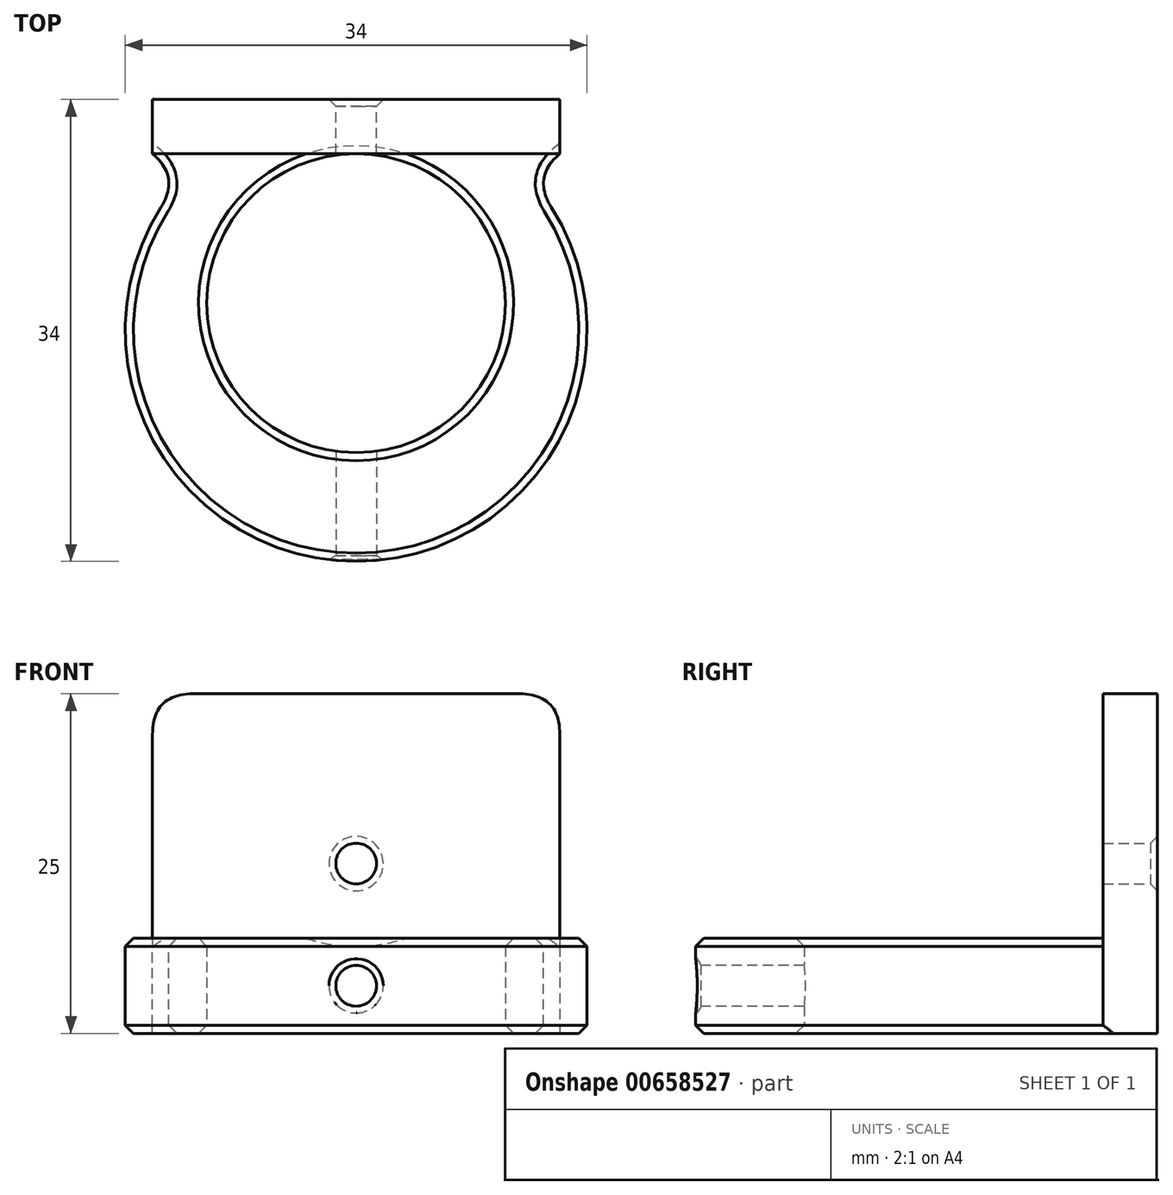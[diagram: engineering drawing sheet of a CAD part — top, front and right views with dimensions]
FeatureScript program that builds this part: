
annotation { "Feature Type Name" : "Feature", "Feature Type Description" : "" }
export const myFeature = defineFeature(function(context is Context, id is Id, definition is map)
    precondition{}
    {
        {
            var Q0;
            Q0=qCreatedBy(makeId("Top.planeOp"),FACE);
            var sketch = newSketch(context, id + "F0", { "sketchPlane" : qUnion([Q0])});
            skCircle(sketch, "E0", {"center": v(0, 0) * mm, "radius": 11 * mm});
            skLineSegment(sketch, "E1.bottom", {"start": v(-15, 15) * mm, "end": v(15, 15) * mm});
            skLineSegment(sketch, "E1.top", {"start": v(-15, 11) * mm, "end": v(15, 11) * mm});
            skLineSegment(sketch, "E1.left", {"start": v(-15, 15) * mm, "end": v(-15, 11) * mm});
            skLineSegment(sketch, "E1.right", {"start": v(15, 15) * mm, "end": v(15, 11) * mm});
            skPoint(sketch, "E2", {"position": v(0, 15) * mm});
            skCircle(sketch, "E3", {"center": v(0, -2) * mm, "radius": 17 * mm});
            skPoint(sketch, "E4", {"position": v(0, -11) * mm});
            skPoint(sketch, "E5", {"position": v(0, -19) * mm});
            skPoint(sketch, "E6", {"position": v(0, 11) * mm});
            skSolve(sketch);
        }
        {
            var Q0;
            {var subQ5=sQuery(id+"F0.wireOp",EDGE,"E1.right");Q0=makeQuery(id+"F0.imprint","IMPRINT",FACE,{"disambiguationData":[TD([[makeQuery(id+"F0.imprint","IMPRINT",EDGE,{"derivedFrom":subQ5}),-1.0]])]});}
            var Q1;
            {var subQ0=sQuery(id+"F0.wireOp",EDGE,"8q8d3DDL-PRP0-A8uf-fQ6a-dR3t6nBeqXp1");var subQ1=makeQuery(id+"F0.imprint","INTERSECT",VERTEX,{"derivedFrom":[subQ0,sQuery(id+"F0.wireOp",EDGE,"E1.bottom")]});Q1=makeQuery(id+"F0.imprint","IMPRINT",FACE,{"disambiguationData":[TD([[makeQuery(id+"F0.imprint","IMPRINT",EDGE,{"disambiguationData":[TD([[subQ1,1.0]])],"derivedFrom":subQ0}),1.0]])]});}
            var Q2;
            {var subQ5=sQuery(id+"F0.wireOp",EDGE,"E1.left");Q2=makeQuery(id+"F0.imprint","IMPRINT",FACE,{"disambiguationData":[TD([[makeQuery(id+"F0.imprint","IMPRINT",EDGE,{"derivedFrom":subQ5}),1.0]])]});}
            var Q3;
            {var subQ0=sQuery(id+"F0.wireOp",EDGE,"E0");Q3=makeQuery(id+"F0.imprint","IMPRINT",FACE,{"disambiguationData":[TD([[makeQuery(id+"F0.imprint","IMPRINT",EDGE,{"derivedFrom":subQ0}),-1.0]])]});}
            var Q4;
            {var subQ0=sQuery(id+"F0.wireOp",EDGE,"E1.top");var subQ1=makeQuery(id+"F0.imprint","INTERSECT",VERTEX,{"derivedFrom":[sQuery(id+"F0.wireOp",EDGE,"E0"),subQ0]});Q4=makeQuery(id+"F0.imprint","IMPRINT",FACE,{"disambiguationData":[TD([[makeQuery(id+"F0.imprint","IMPRINT",EDGE,{"disambiguationData":[TD([[subQ1,1.0]])],"derivedFrom":subQ0}),1.0]])]});}
            extrude(context, id + "F1", {"entities" : qUnion([Q0, Q1, Q2, Q3, Q4]), "depth" : 7 * mm, "offsetDistance" : 25 * mm});
        }
        {
            var Q0;
            Q0=makeQuery(id+"F1.opExtrude","CAP_FACE",FACE,{"disambiguationData":[OSD([sQuery(id+"F0.wireOp",EDGE,"E0"),sQuery(id+"F0.wireOp",EDGE,"8q8d3DDL-PRP0-A8uf-fQ6a-dR3t6nBeqXp1"),sQuery(id+"F0.wireOp",EDGE,"E1.bottom"),sQuery(id+"F0.wireOp",EDGE,"E1.top"),sQuery(id+"F0.wireOp",EDGE,"E1.left"),sQuery(id+"F0.wireOp",EDGE,"E1.right")])],"isStart":false});
            var sketch = newSketch(context, id + "F2", { "sketchPlane" : qUnion([Q0])});
            skLineSegment(sketch, "E7.0", {"start": v(-15, 15) * mm, "end": v(15, 15) * mm});
            skLineSegment(sketch, "E8.0", {"start": v(15, 15) * mm, "end": v(15, 11) * mm});
            skLineSegment(sketch, "E9.0", {"start": v(-15, 11) * mm, "end": v(15, 11) * mm});
            skLineSegment(sketch, "E10.0", {"start": v(-15, 15) * mm, "end": v(-15, 11) * mm});
            skSolve(sketch);
        }
        {
            var Q0;
            Q0=makeQuery(id+"F2.imprint","IMPRINT",FACE,{"disambiguationData":[TD([[makeQuery(id+"F2.imprint","IMPRINT",EDGE,{"derivedFrom":sQuery(id+"F2.wireOp",EDGE,"E7.0")}),-1.0]])]});
            extrude(context, id + "F3", {"entities" : qUnion([Q0]), "operationType" : NewBodyOperationType.ADD, "depth" : 18 * mm, "offsetDistance" : 25 * mm});
        }
        {
            var Q0;
            Q0=qCreatedBy(makeId("Front.planeOp"),FACE);
            cPlane(context, id + "F4", {"entities" : qUnion([Q0]), "cplaneType" : CPlaneType.OFFSET, "offset" : 19 * mm, "width" : 150 * mm, "height" : 150 * mm});
        }
        {
            var Q0;
            Q0=qCreatedBy(id+"F4.planeOp",FACE);
            var sketch = newSketch(context, id + "F5", { "sketchPlane" : qUnion([Q0])});
            skLineSegment(sketch, "E11", {"start": v(-17, 0) * mm, "end": v(-17, 7) * mm});
            skLineSegment(sketch, "E12", {"start": v(17, 7) * mm, "end": v(17, 0) * mm});
            skLineSegment(sketch, "E13.0", {"start": v(-17, 7) * mm, "end": v(17, 7) * mm});
            skLineSegment(sketch, "E14.0", {"start": v(-17, 0) * mm, "end": v(17, 0) * mm});
            skPoint(sketch, "E15", {"position": v(0, 3.5) * mm});
            skSolve(sketch);
        }
        {
            var Q0;
            Q0=sQuery(id+"F5.wireOp",VERTEX,"E15");
            var Q1;
            Q1=makeQuery(id+"F1.opExtrude","SWEPT_BODY",BODY,{"disambiguationData":[OSD([sQuery(id+"F0.wireOp",EDGE,"E0"),sQuery(id+"F0.wireOp",EDGE,"E1.bottom"),sQuery(id+"F0.wireOp",EDGE,"E1.top"),sQuery(id+"F0.wireOp",EDGE,"E1.left"),sQuery(id+"F0.wireOp",EDGE,"E1.right"),sQuery(id+"F0.wireOp",EDGE,"E3")])]});
            hole(context, id + "F6", {"style" : HoleStyle.C_SINK, "endStyle" : HoleEndStyle.BLIND, "holeDiameter" : 3 * mm, "cSinkDiameter" : 4 * mm, "cSinkAngle" : 120 * degree, "majorDiameter" : 5 * mm, "holeDepth" : 10 * mm, "isTappedThrough" : true, "tappedDepth" : 12 * mm, "tapClearance" : 3, "locations" : qUnion([Q0]), "scope" : qUnion([Q1])});
        }
        {
            var Q0;
            {var subQ0=sQuery(id+"F0.wireOp",EDGE,"E3");var subQ1=sQuery(id+"F0.wireOp",EDGE,"E1.top");Q0=makeQuery(id+"F1.opExtrude","SWEPT_EDGE",EDGE,{"disambiguationData":[OSD([subQ1,subQ0]),TDD([makeQuery(id+"F0.imprint","INTERSECT",VERTEX,{"disambiguationData":[OD(1.0)],"derivedFrom":[subQ1,subQ0]})])]});}
            var Q1;
            {var subQ0=sQuery(id+"F0.wireOp",EDGE,"E3");var subQ1=sQuery(id+"F0.wireOp",EDGE,"E1.top");Q1=makeQuery(id+"F1.opExtrude","SWEPT_EDGE",EDGE,{"disambiguationData":[OSD([subQ1,subQ0]),TDD([makeQuery(id+"F0.imprint","INTERSECT",VERTEX,{"disambiguationData":[OD(0.0)],"derivedFrom":[subQ1,subQ0]})])]});}
            var Q2;
            Q2=makeQuery(id+"F3.opExtrude","CAP_EDGE",EDGE,{"disambiguationData":[OSD([sQuery(id+"F2.wireOp",EDGE,"E10.0")])],"isStart":false});
            var Q3;
            Q3=makeQuery(id+"F3.opExtrude","CAP_EDGE",EDGE,{"disambiguationData":[OSD([sQuery(id+"F2.wireOp",EDGE,"E8.0")])],"isStart":false});
            var Q4;
            Q4=makeQuery(id+"F3.boolean.opBoolean","SPLIT",EDGE,{"disambiguationData":[OD(0.0)],"derivedFrom":makeQuery(id+"F3.opExtrude","CAP_EDGE",EDGE,{"disambiguationData":[OSD([sQuery(id+"F2.wireOp",EDGE,"E9.0")])],"isStart":true})});
            var Q5;
            Q5=makeQuery(id+"F3.boolean.opBoolean","SPLIT",EDGE,{"disambiguationData":[OD(1.0)],"derivedFrom":makeQuery(id+"F3.opExtrude","CAP_EDGE",EDGE,{"disambiguationData":[OSD([sQuery(id+"F2.wireOp",EDGE,"E9.0")])],"isStart":true})});
            fillet(context, id + "F7", {"entities" : qUnion([Q0, Q1, Q2, Q3, Q4, Q5]), "radius" : 3 * mm, "tangentPropagation" : true, "rho" : 0.5, "crossSection" : FilletCrossSection.CONIC, "allowEdgeOverflow" : false});
        }
        {
            var Q0;
            Q0=makeQuery(id+"F1.opExtrude","CAP_EDGE",EDGE,{"disambiguationData":[OSD([sQuery(id+"F0.wireOp",EDGE,"E0")])],"isStart":true});
            var Q1;
            Q1=makeQuery(id+"F1.opExtrude","CAP_EDGE",EDGE,{"disambiguationData":[OSD([sQuery(id+"F0.wireOp",EDGE,"E0")])],"isStart":false});
            var Q2;
            Q2=makeQuery(id+"F1.opExtrude","CAP_EDGE",EDGE,{"disambiguationData":[OSD([sQuery(id+"F0.wireOp",EDGE,"E3")])],"isStart":true});
            var Q3;
            Q3=makeQuery(id+"F1.opExtrude","CAP_EDGE",EDGE,{"disambiguationData":[OSD([sQuery(id+"F0.wireOp",EDGE,"E3")])],"isStart":false});
            chamfer(context, id + "F8", {"entities" : qUnion([Q0, Q1, Q2, Q3]), "width" : 0.6 * mm, "tangentPropagation" : true});
        }
        {
            var Q0;
            Q0=makeQuery(id+"F3.boolean.opBoolean","MERGE",FACE,{"derivedFrom":[makeQuery(id+"F1.opExtrude","SWEPT_FACE",FACE,{"disambiguationData":[OSD([sQuery(id+"F0.wireOp",EDGE,"E1.bottom")])]}),makeQuery(id+"F3.opExtrude","SWEPT_FACE",FACE,{"disambiguationData":[OSD([sQuery(id+"F2.wireOp",EDGE,"E7.0")])]})]});
            var sketch = newSketch(context, id + "F9", { "sketchPlane" : qUnion([Q0])});
            skPoint(sketch, "E16", {"position": v(0, 12.5) * mm});
            skLineSegment(sketch, "E17.0.0", {"start": v(12, 25) * mm, "end": v(-12, 25) * mm});
            skFitSpline(sketch, "E17.0.1", {"points": [v(-12, 25) * mm, v(-14, 25) * mm, v(-15, 24) * mm, v(-15, 22) * mm]});
            skLineSegment(sketch, "E17.0.2", {"start": v(-15, 22) * mm, "end": v(-15, 0) * mm});
            skLineSegment(sketch, "E17.0.3", {"start": v(-15, 0) * mm, "end": v(15, 0) * mm});
            skLineSegment(sketch, "E17.0.4", {"start": v(15, 0) * mm, "end": v(15, 22) * mm});
            skFitSpline(sketch, "E17.0.5", {"points": [v(15, 22) * mm, v(15, 24) * mm, v(14, 25) * mm, v(12, 25) * mm]});
            skLineSegment(sketch, "E18", {"start": v(-15, 25) * mm, "end": v(15, 0) * mm});
            skLineSegment(sketch, "E19", {"start": v(-15, 0) * mm, "end": v(15, 25) * mm});
            skSolve(sketch);
        }
        {
            var Q0;
            Q0=sQuery(id+"F9.wireOp",VERTEX,"E16");
            var Q1;
            Q1=makeQuery(id+"F1.opExtrude","SWEPT_BODY",BODY,{"disambiguationData":[OSD([sQuery(id+"F0.wireOp",EDGE,"E0"),sQuery(id+"F0.wireOp",EDGE,"E1.bottom"),sQuery(id+"F0.wireOp",EDGE,"E1.top"),sQuery(id+"F0.wireOp",EDGE,"E1.left"),sQuery(id+"F0.wireOp",EDGE,"E1.right"),sQuery(id+"F0.wireOp",EDGE,"E3")])]});
            hole(context, id + "F10", {"style" : HoleStyle.C_SINK, "endStyle" : HoleEndStyle.THROUGH, "holeDiameter" : 3 * mm, "cSinkDiameter" : 4 * mm, "cSinkAngle" : 90 * degree, "majorDiameter" : 5 * mm, "isTappedThrough" : true, "tappedDepth" : 12 * mm, "tapClearance" : 3, "startFromSketch" : true, "locations" : qUnion([Q0]), "scope" : qUnion([Q1])});
        }
    });
